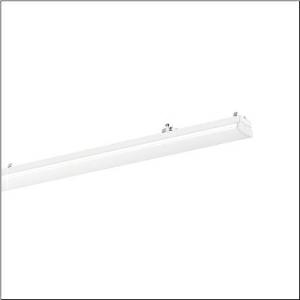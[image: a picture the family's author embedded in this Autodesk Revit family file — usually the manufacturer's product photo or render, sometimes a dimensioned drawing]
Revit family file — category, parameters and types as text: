
# Revit family: licross_21_recessed_opal_mo_52te1d7n44xg
name_source: partatom
category: Lighting Fixtures
units: mm (PartAtom-declared; Revit-internal decimal feet)

## family parameters
Cut with Voids When Loaded = No
Host = Face
Light Source = No
Part Type = Normal
Room Calculation Point = No
Round Connector Dimension = Use Diameter
Shared = No

## types (1)
- Licross 21 recessed opal MO (1 x LED, 4400 lm, 24.7 W, 4000K)
    Apparent Load = 25 VA
    CIE Flux Codes = 44 73 91 87 100
    Color Rendering = 80
    Color Temperature = 4000K
    Default Elevation = 1800 mm
    Description = Licross 21 recessed opal MO, luminaire insert, of sheet steel, galvanised, coil coated, white, length: 1.500mm, width: 66mm, height: 67mm, LED rated luminous flux: 4.400lm, light colour: 840, SDCM (Standard Deviation of Colour Matching)MacAdam ≤ 3 SDCM (initial), control gear: ON/OFF, with plug, 3-pole, with phase selection, mains connection: 220..240V, AC, 50/60Hz, rated input power: 25W, internal wiring halogen-free, primary optical cover: cover, of PMMA, light emission: direct with ceiling illumination distribution, primary light characteristic: symmetric, protection rating (complete): IP54, insulation class (complete): insulation class I (protective earthing), certification: CE, ENEC, VDE, UKCA, protection symbol: D if used in an environment with non-conductive dust loads with corresponding accessories, impact resistance: IK06, permissible ambient temperature for indoor applications: -35..+50°C, corresponds to IFS (International Featured Standards) requirements for safety and quality in the food industry, reducing of maximum allowable ambient temperature of 5°C with ceiling mounting, LABS conformity tested according to VDMA 24364:2018-05, The light source and the operating device comply with the requirements of the Ecodesign Regulation (EU) 2019/2020 and are replaceable in accordance with this regulation, packaging unit: 1 piece
    Height = 83 mm
    Lamp = 1 x LED
    Lamp Light Flux = 4400 lm
    Lamp Power = 24.7 W
    Lamp count = 1
    Length = 1500 mm
    Luminous efficacy = 178 lm/W
    Manufacturer = Siteco
    ModVariant = No
    Model = 52TE1D7N44XG
    Mounting Place = Ceiling
    Mounting Type = Pendant
    Number of Poles = 1
    OnlyDefault = Yes
    Power Factor = 1
    Product Name = Licross 21 recessed opal MO
    Product group = luminaire insert | ceiling pendant
    ProductGroupID = 901
    Protection Class = Protection class I
    Protection Degree = IP 54
    RLX_Detail_Level = 1
    RLX_Emergency_Light_Flux = 0 lm
    RLX_Emergency_Type = 0
    RLX_Emergency_Type_DB = No
    RlxData = <blob elided: 23409 chars, md5=b64ce278>
    Socket = socket
    Standby Power = 0 W
    System Light Flux = 4400 lm
    System Power = 25 W
    Type Comments = Product without accessories
    Type Image = l_1313666.jpg
    URL = http://relux.com
    VarID = ---
    Voltage = 0 V
    Weight = 0.00 kg
    Width = 76 mm

## geometry (parser evidence)
native form markers: Blend x4, Sweep x15
no freeform markers — native parametric forms only
